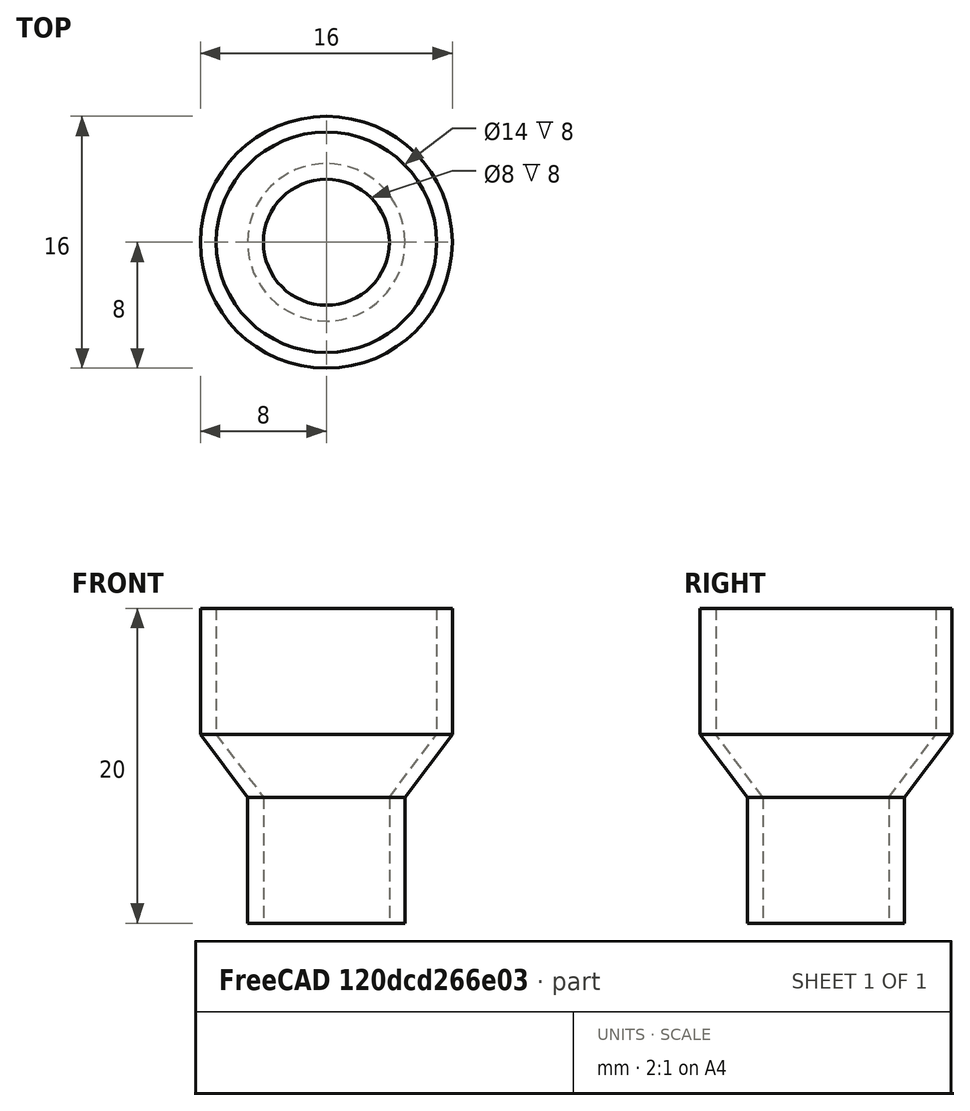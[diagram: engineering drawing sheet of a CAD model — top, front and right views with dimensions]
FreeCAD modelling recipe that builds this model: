
FCSTD DOCUMENT  (FreeCAD 1.0R38641 +468 (Git))
Label: Body2
License: All rights reserved
LicenseURL: https://en.wikipedia.org/wiki/All_rights_reserved
objects: Sketcher::SketchObject×1, PartDesign::Revolution×1, PartDesign::Body×1
note: 6 computed .brp shape members not serialized (recipe doc carries the construction recipe); baked Part::Feature solids carry a one-line shape summary decoded from their .brp

FEATURE [Sketcher::SketchObject] Sketch
  ArcFitTolerance = 1e-06
  AttachmentSupport = -> [XZ_Plane]
  FullyConstrained = true
  MakeInternals = false
  MapMode = 5
  Placement = pos=(0,0,0) rot=(1,0,0;1.5708rad)
  sketch-geometry (8):
    g0: LineSegment StartX=-8 StartY=20 StartZ=0 EndX=-7 EndY=20 EndZ=0
    g1: LineSegment StartX=-7 StartY=20 StartZ=0 EndX=-7 EndY=12 EndZ=0
    g2: LineSegment StartX=-7 StartY=12 StartZ=0 EndX=-4 EndY=8 EndZ=0
    g3: LineSegment StartX=-4 StartY=8 StartZ=0 EndX=-4 EndY=0 EndZ=0
    g4: LineSegment StartX=-4 StartY=0 StartZ=0 EndX=-5 EndY=0 EndZ=0
    g5: LineSegment StartX=-5 StartY=0 StartZ=0 EndX=-5 EndY=8 EndZ=0
    g6: LineSegment StartX=-5 StartY=8 StartZ=0 EndX=-8 EndY=12 EndZ=0
    g7: LineSegment StartX=-8 StartY=12 StartZ=0 EndX=-8 EndY=20 EndZ=0
  constraints (24):
    c: Coincident(g0,g1)
    c: Coincident(g1,g2)
    c: Coincident(g2,g3)
    c: PointOnObject(g3,g-1)
    c: Coincident(g3,g4)
    c: PointOnObject(g4,g-1)
    c: Coincident(g4,g5)
    c: Coincident(g5,g6)
    c: Coincident(g6,g7)
    c: Coincident(g7,g0)
    c: Vertical(g7)
    c: Equal(g4,g0)
    c: Horizontal(g0)
    c: Parallel(g7,g1)
    c: Parallel(g6,g2)
    c: Parallel(g5,g3)
    c: DistanceX(g4,g4) = 1
    c: DistanceX(g4,g-1) = 5
    c: Distance(g0,g-2) = 8
    c: Vertical(g3)
    c: DistanceY(g3,g3) = 8
    c: DistanceY(g1,g1) = 8
    c: Equal(g3,g5)
    c: DistanceY(g3,g0) = 20
FEATURE [PartDesign::Revolution] Revolution
  Angle = 360
  Angle2 = 60
  Axis = (0,2e-16,1)
  Base = (0,0,0)
  Placement = pos=(0,0,0) rot=(1,0,0;1.5708rad)
  Profile = -> Sketch
  ReferenceAxis = -> Sketch [V_Axis]
  Refine = true
  Suppressed = false
  Type = 0
FEATURE [PartDesign::Body] Body
  AllowCompound = false
  Group = -> [Sketch,Revolution]
  Origin = -> Origin
  Tip = -> Revolution
